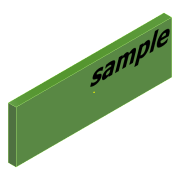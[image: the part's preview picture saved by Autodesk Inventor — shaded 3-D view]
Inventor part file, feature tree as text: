
AUTODESK INVENTOR PART (.ipt)
format: ipt  version: 2021 (Build 250183000, 183)  size: 81,920 bytes
history: native  units: mm
features: sketch x2, other x1, extrude x1
ambient origin geometry x8: Origin, YZ Plane, XZ Plane, XY Plane, X Axis, Y Axis, Z Axis, Center Point
bodies: Body1 (feature_tree)
feature tree (4):
  other  "Твердое тело1"
  extrude  "Выдавливание1"  Depth=30.0mm
  sketch  "Эскиз2"
  sketch  "Эскиз1"
